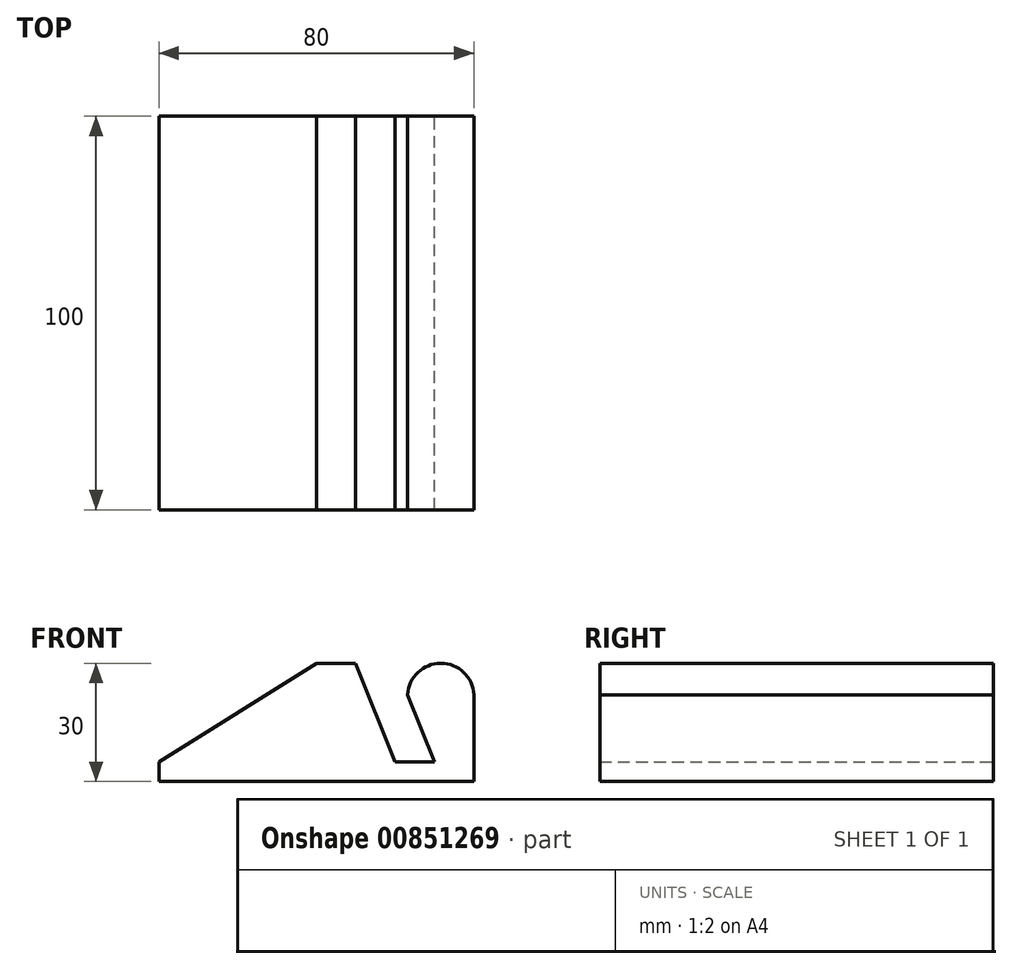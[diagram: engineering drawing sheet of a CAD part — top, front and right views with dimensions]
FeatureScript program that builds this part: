
annotation { "Feature Type Name" : "Feature", "Feature Type Description" : "" }
export const myFeature = defineFeature(function(context is Context, id is Id, definition is map)
    precondition{}
    {
        {
            var Q0;
            Q0=qCreatedBy(makeId("Front.planeOp"),FACE);
            var sketch = newSketch(context, id + "F0", { "sketchPlane" : qUnion([Q0])});
            skLineSegment(sketch, "E0.bottom", {"start": v(-20, -5) * mm, "end": v(20, -5) * mm});
            skLineSegment(sketch, "E0.top", {"start": v(-20, 25) * mm, "end": v(-10, 25) * mm});
            skLineSegment(sketch, "E0.left", {"start": v(-20, -5) * mm, "end": v(-20, 25) * mm, "construction": true});
            skLineSegment(sketch, "E0.right", {"start": v(20, -5) * mm, "end": v(20, 17) * mm});
            skLineSegment(sketch, "E1", {"start": v(-10, 25) * mm, "end": v(0, 0) * mm});
            skLineSegment(sketch, "E2", {"start": v(0, 0) * mm, "end": v(10, 0) * mm});
            skLineSegment(sketch, "E3", {"start": v(10, 0) * mm, "end": v(0, 25) * mm});
            skPoint(sketch, "E3.endSnap0", {"position": v(0, 25) * mm});
            skArc(sketch, "E4", {"start": v(20, 17) * mm, "mid": v(11.6, 25) * mm, "end": v(3.2, 17) * mm});
            skLineSegment(sketch, "E5.trimOffspring", {"start": v(0, 25) * mm, "end": v(0, 25) * mm});
            skPoint(sketch, "E6.orphan", {"position": v(20, 25) * mm});
            skLineSegment(sketch, "E7", {"start": v(-20, -5) * mm, "end": v(-60, -5) * mm});
            skLineSegment(sketch, "E8", {"start": v(-60, -5) * mm, "end": v(-60, 0) * mm});
            skLineSegment(sketch, "E9", {"start": v(-60, 0) * mm, "end": v(-20, 25) * mm});
            skSolve(sketch);
        }
        {
            var Q0;
            Q0=makeQuery(id+"F0.imprint","IMPRINT",FACE,{"disambiguationData":[TD([[makeQuery(id+"F0.imprint","IMPRINT",EDGE,{"derivedFrom":sQuery(id+"F0.wireOp",EDGE,"E0.bottom")}),1.0]])]});
            extrude(context, id + "F1", {"entities" : qUnion([Q0]), "endBound" : BoundingType.SYMMETRIC, "depth" : 100 * mm, "offsetDistance" : 25 * mm});
        }
    });
